# Revit family: PRD_AR_WlHngUrnls_Urinal_CMPX538E,CMPX538RS,CMPX538WF
name_source: partatom
category: Plumbing Fixtures
revit_build: Autodesk Revit 2018 (Build: 20190510_1515(x64)
units: mm (PartAtom-declared; Revit-internal decimal feet)

## family parameters
Cut with Voids When Loaded = No
Host = Face
OmniClass Number = 23.45.05.21.11.21
OmniClass Title = Urinals
Part Type = Normal
Room Calculation Point = No
Round Connector Dimension = Use Diameter
Shared = No

## types (3) — shared parameters
AssetType = Fixed
Category = Pr_40_20_93_82, Wall-hung urinals
Default Elevation = 650 mm  [stored 2.13255 ft]
DiameterNominal = 15  [stored 0.0492126 ft]
DurationUnit = year
Features = stainless steel, 1.20 mm, satin finished, wall mounting, 313x732x341 mm (WxHxD)
Finish = Satin finished
Flow = 0.0 L/s
Form = Wall hung
IfcExportAs = IfcSanitaryTerminalType
IfcExportType = URINAL
InletSize = DN15
IntegralAccessories = Included wall fixing bolts, siphon
Manufacturer = KWC Group AG
ManufacturerName = KWC Group AG
ManufacturerURL = www.kwc.com
Material = PRD_AR_StainlessSteel_SatinFinished
MaterialsBody = Stainless steel 1.4301
MaterialsFinishAndColour = Stainless steel, satin finished
NBSDescription = Wall hung urinals
NBSReference = 45-35-70/350
NominalDepth = 341 mm
NominalHeight = 732 mm
NominalLength = 732 mm
NominalWidth = 313 mm  [stored 1.0269 ft]
ProductInformation = https://pim.kwc.com
SensorMaterial = <By Category>
Size = 313 x 732 x 341 mm
SpilloverLevel = 650 mm  [stored 2.13255 ft]
TypeOfMounting = Wall-Mounting
TypeOfUrinal = Single-Urinal
URL = www.kwc.com
Uniclass2015Code = Pr_40_20_93_82
Uniclass2015Title = Wall-hung urinals
Uniclass2015Version = Products v1.7
UrinalColor = Stainless steel
UrinalMaterial = Stainless steel
UrinalType = Bowl
Version = 1
WarrantyDurationUnit = year
WasteSize = 50  [stored 0.164042 ft]
WaterSupplyOverflowAndWasteHolesOverflow = None
WaterSupplyOverflowAndWasteHolesWaste = Concealed
WaterSupplyOverflowAndWasteHolesWaterSupply = Concealed

## per-type parameters (varying)
| type | BIMObjectName | Description | GrossWeight | Input Supply Voltage V | ModelNumber | Name | NetWeight | Power | ProtectiveSystemIP | Type | TypeOfFlushing | TypeOfWasteKit | Visible 1 | Visible 2 |
| CMPX538RS | PRD_AR_WallHungUrinals_Urinal_CMPX538RS | Single urinal for wall mounting, stainless steel, surface satin finished, material thickness 1.2 mm, oval bowl, hidden horizontal outlet towards wall, mounting and fixing conform to EN 80, hidden screws, included trap DN 50, included mounting bracket and domed waste. with stainless steel spreader 1/2" and ring sensor | 10.00 kg | 24 V DC | 2000103380 | Urinal CMPX538RS | 8.50 kg | 7 W | IP40 | CMPX538,CMPX538RS,CMPX538WF : CMPX538 | Water | Perforated | Yes | No |
| CMPX538WF | PRD_AR_WallHungUrinals_Urinal_CMPX538WF | Single urinal for wall mounting, stainless steel, surface satin finished, material thickness 1.2 mm, oval bowl, hidden horizontal outlet towards wall, mounting and fixing conform to EN 80, hidden screws, included trap DN 50, included mounting bracket and domed waste. Waterfree urinal, with 90° elbow DN 50, inclusive stainless steel waste and membrane. | 8.74 kg |  | 2000071875 | Urinal CMPX538WF | 7.22 kg |  |  | CMPX538,CMPX538RS,CMPX538WF : CMPX538 | Water-Free | WF-Flat-Perforated | No | No |
| CMPX538E | PRD_AR_WallHungUrinals_Urinal_CMPX538E | Single urinal for wall mounting, stainless steel, surface satin finished, material thickness 1.2 mm, oval bowl, hidden horizontal outlet towards wall, mounting and fixing conform to EN 80, hidden screws, included trap DN 50, included mounting bracket and domed waste. with stainless steel spreader 1/2", for exposed cistern and waste pipework | 9.00 kg |  | 2000100769 | Urinal CMPX538E | 9.00 kg |  |  | CMPX538E | Water | Dome | Yes | Yes |

note: column(s) folded — value = type name in every type: Model, ModelReference

note: [stored X ft] marks values corroborated as IEEE doubles in the binary element streams (Revit-internal decimal feet)

## geometry (parser evidence)
native form markers: Sweep x3
no freeform markers — native parametric forms only
